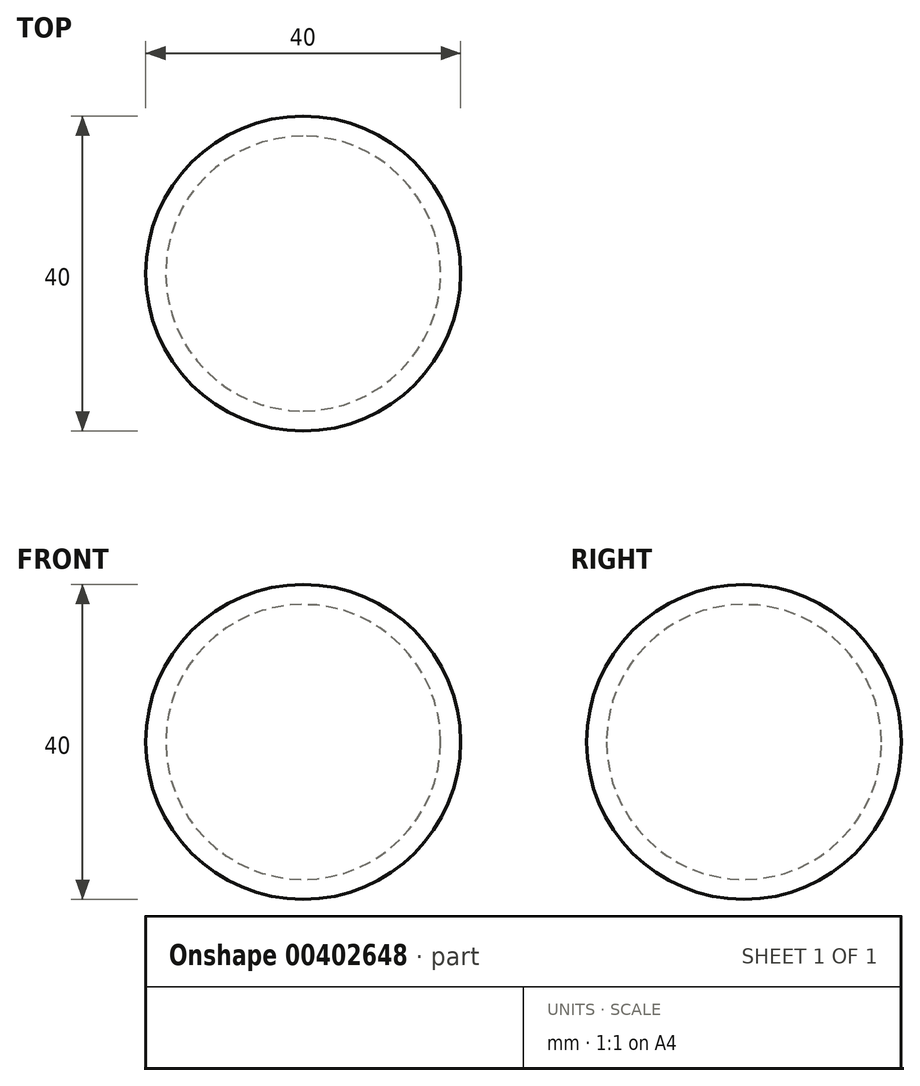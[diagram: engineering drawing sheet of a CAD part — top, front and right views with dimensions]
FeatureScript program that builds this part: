
annotation { "Feature Type Name" : "Feature", "Feature Type Description" : "" }
export const myFeature = defineFeature(function(context is Context, id is Id, definition is map)
    precondition{}
    {
        {
            var Q0;
            Q0=qCreatedBy(makeId("Top.planeOp"),FACE);
            var sketch = newSketch(context, id + "F0", { "sketchPlane" : qUnion([Q0])});
            skArc(sketch, "E0", {"start": v(0, 20) * mm, "mid": v(-20, 0) * mm, "end": v(0, -20) * mm});
            skLineSegment(sketch, "E1", {"start": v(0, 24.53) * mm, "end": v(0, -23.34) * mm});
            skSolve(sketch);
        }
        {
            var Q0;
            {var subQ0=sQuery(id+"F0.wireOp",EDGE,"E0");Q0=makeQuery(id+"F0.imprint","IMPRINT",FACE,{"disambiguationData":[TD([[makeQuery(id+"F0.imprint","IMPRINT",EDGE,{"derivedFrom":subQ0}),1.0]])]});}
            var Q1;
            Q1=sQuery(id+"F0.wireOp",EDGE,"E1");
            revolve(context, id + "F1", {"entities" : qUnion([Q0]), "axis" : qUnion([Q1]), "revolveType" : RevolveType.FULL});
        }
        {
            var Q0;
            Q0=makeQuery(id+"F1.opRevolve","SWEPT_FACE",FACE,{"disambiguationData":[OSD([sQuery(id+"F0.wireOp",EDGE,"E0")])]});
            var Q1;
            Q1=makeQuery(id+"F1.opRevolve","SWEPT_BODY",BODY,{"disambiguationData":[OSD([sQuery(id+"F0.wireOp",EDGE,"E0"),sQuery(id+"F0.wireOp",EDGE,"E1")])]});
            shell(context, id + "F2", {"isHollow" : true, "entities" : qUnion([Q0]), "parts" : qUnion([Q1]), "thickness" : 2.54 * mm});
        }
    });
